# Revit family: Sink-Single Bowl-Clark Polar Under Over Mount1
name_source: partatom
category: Plumbing Fixtures
revit_build: Autodesk Revit 2014 (Build: 20131024_2115(x64)
units: mm (PartAtom-declared; Revit-internal decimal feet)

## types (1)
- Polar
    Assembly Code = D2010410
    CW Connection = No
    Capacity_ANZRS = 26.0 L
    Cost = 0 $
    Default Elevation = 0 mm  [stored 0 ft]
    Depth_ANZRS = 205 mm  [stored 0.672572 ft]
    Description = 304 Grade Stainless Steel.  Polished Finish.  Includes Basket Waste A0084
    HW Connection = No
    Keynote = SK
    Length_ANZRS = 405 mm
    Manufacturer = GWA Bathrooms & Kitchens
    Material_ANZRS = Metal-Stainless-Caroma
    Model = PPL10B
    ModifiedIssue_ANZRS = 20150114 $
    Type Comments = Clark Polar Single Bowl Undermount/Overmount Sink
    URL = http://www.clark.com.au
    Vent Connection = No
    WFU = 2
    Waste Connection = Yes
    Waste Radius = 25 mm  [stored 0.082021 ft]
    Width_ANZRS = 455 mm

note: [stored X ft] marks values corroborated as IEEE doubles in the binary element streams (Revit-internal decimal feet)

## geometry (parser evidence)
native form markers: Blend x6, Sweep x2
no freeform markers — native parametric forms only
